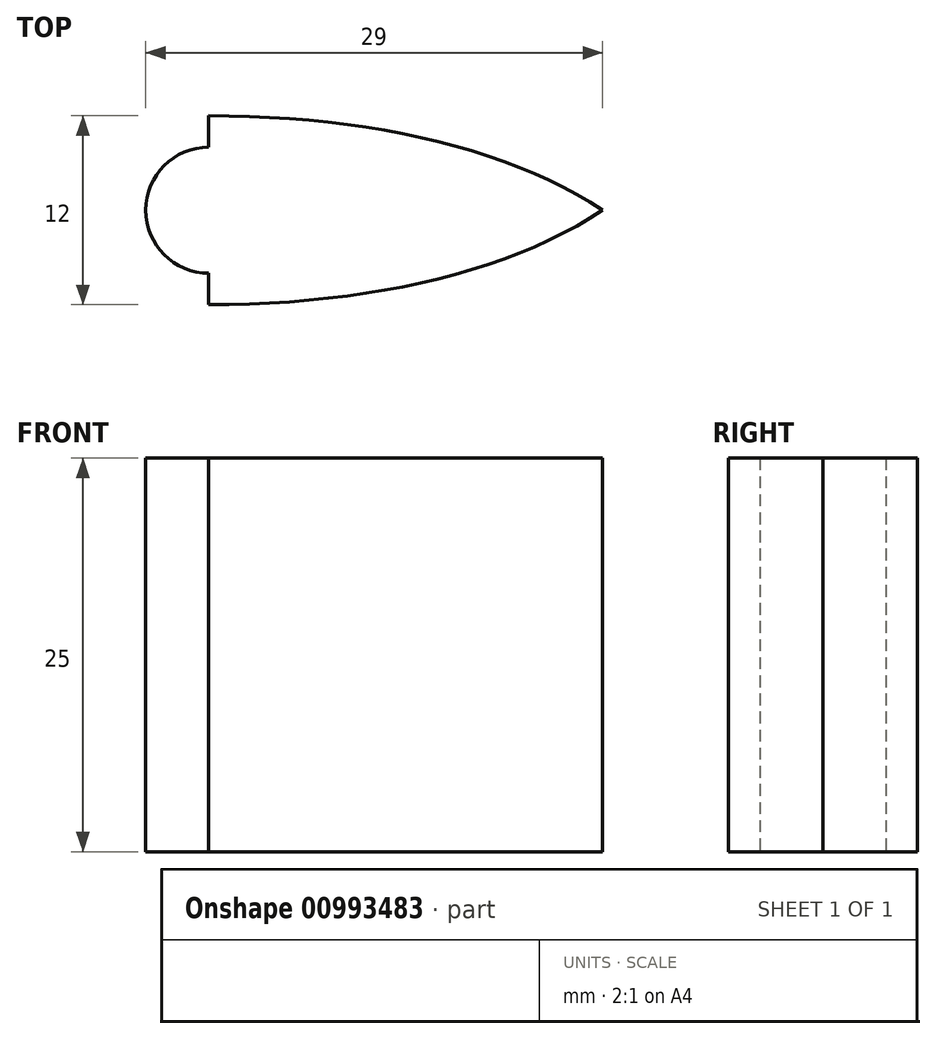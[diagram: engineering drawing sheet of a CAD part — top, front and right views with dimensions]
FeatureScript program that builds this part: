
annotation { "Feature Type Name" : "Feature", "Feature Type Description" : "" }
export const myFeature = defineFeature(function(context is Context, id is Id, definition is map)
    precondition{}
    {
        {
            var Q0;
            Q0=qCreatedBy(makeId("Top.planeOp"), FACE);
            var sketch = newSketch(context, id + "F0", { "sketchPlane" : qUnion([Q0])});
            skArc(sketch, "E0", {"start": v(0, 4) * mm, "mid": v(-4, 0) * mm, "end": v(0, -4) * mm});
            skLineSegment(sketch, "E1", {"start": v(0, 6) * mm, "end": v(0, 4) * mm});
            skPoint(sketch, "E2", {"position": v(25, 0) * mm});
            skLineSegment(sketch, "E3", {"start": v(0, 6) * mm, "end": v(-8.85, 6) * mm, "construction": true});
            skLineSegment(sketch, "E4", {"start": v(25, 0) * mm, "end": v(25, -17) * mm, "construction": true});
            skFitSpline(sketch, "E5", {"points": [v(0, 6) * mm, v(25, 0) * mm], "startDerivative": vector(30, 0) * mm, "endDerivative": vector(18, -12) * mm});
            skLineSegment(sketch, "E6", {"start": v(0, 0) * mm, "end": v(-12.62, 0) * mm, "construction": true});
            skFitSpline(sketch, "E7.MirrorCS", {"points": [v(0, -6) * mm, v(25, 0) * mm], "startDerivative": vector(30, 0) * mm, "endDerivative": vector(18, 12) * mm});
            skLineSegment(sketch, "E8.trimOffspring", {"start": v(0, -4) * mm, "end": v(0, -6) * mm});
            skSolve(sketch);
        }
        {
            var Q0;
            Q0 = qSketchRegion(id + "F0", true);
            extrude(context, id + "F1", {"entities" : qUnion([Q0]), "domain" : OperationDomain.MODEL, "flatOperationType" : FlatOperationType.REMOVE, "depth" : 25 * mm, "offsetDistance" : 25 * mm});
        }
    });
